# Revit family: NTO_ACCS_MorseTableAccessories-MA
name_source: partatom
category: Furniture
units: mm (PartAtom-declared; Revit-internal decimal feet)

## family parameters
Always vertical = Yes
Cut with Voids When Loaded = No
Enable Cutting in Views = No
OmniClass Number = 23.40.20.00
OmniClass Title = General Furniture and Specialties
Render Appearance Source = Family Geometry
Room Calculation Point = No
Shared = No
Work Plane-Based = Yes

## types (5) — shared parameters
AssetType = Movable
BIMObjectName = NTO_Morse_WorkTable
Category = Pr_65_70_11 : Cable management and accessories
Color = Available in 16 RALs
DurationUnit = year
ExpectedLife = 10
Features = Available in 16 RALs
Finish = Available in 16 RALs
IfcExportAs = IfcFurnitureType
IfcExportType = Table
MainColor = Available in 16 RALs
Manufacturer = NaughtOne
ManufacturerName = NaughtOne
ManufacturerURL = www.naughtone.com
Material = Available in 16 RALs
NBSDescription = Table
NBSReference = 45-35-72/352
ProductInformation = www.naughtone.com/product/morse/
Shape = Rectangular
URL = www.naughtone.com
Uniclass2015Code = Pr_65_70_11
Uniclass2015Title = Cable management and accessories
Uniclass2015Version = Products v1.30
Version = 1
WarrantyDescription = 10 Years
WarrantyDurationUnit = year
zero-valued in all types: Default Elevation

## per-type parameters (varying)
| type | Description | Dot Material | MABKE | MADOTS | MADOTT | MADSHS | MADVD | Model | ModelNumber | ModelReference | Name | NominalHeight | NominalLength | NominalWidth | Size | Type Comments |
| NTO_MorseTableAccessoriesCableManagementSmall_MADOTT | Morse Table Accessories - Cable Managment Small | NTO_Finish_PowderCoatOrange | No | No | Yes | No | No | MADOTT | MADOTT | Morse Table Accessories - Cable Managment Small | Morse Table Accessories - Cable Managment Small | 60 mm  [stored 0.19685 ft] | 70 mm  [stored 0.229659 ft] | 70 mm  [stored 0.229659 ft] | 70 x 70 x 60 mm | Morse Table Accessories - Cable Managment Small |
| NTO_MorseTableAccessoriesCableManagementLarge_MADOTS | Morse Table Accessories - Cable Managment Large | NTO_Finish_PowderCoatBlue | No | Yes | No | No | No | MADOTS | MADOTS | Morse Table Accessories - Cable Managment Large | Morse Table Accessories - Cable Managment Large | 100 mm  [stored 0.328084 ft] | 125 mm  [stored 0.410105 ft] | 125 mm  [stored 0.410105 ft] | 125 x 125 x 100 mm | Morse Table Accessories - Cable Managment Large |
| NTO_MorseTableAccessoriesCableManagementPillShaped_MADSHS | Morse Table Accessories - Cable Managment Pill Shaped | NTO_Finish_PowderCoatGrey | No | No | No | Yes | No | MADSHS | MADSHS | Morse Table Accessories - Cable Managment Pill Shaped | Morse Table Accessories - Cable Managment Pill Shaped | 70 mm  [stored 0.229659 ft] | 550 mm | 200 mm  [stored 0.656168 ft] | 550 x 250 x 70 mm | Morse Table Accessories - Cable Managment Pill Shaped |
| NTO_MorseTableAccessoriesPartitionPinBoard_MADVD | Morse Table Accessories - Partition Pin Board | NTO_Finish_PowderCoatGrey | No | No | No | No | Yes | MADVD | MADVD | Morse Table Accessories - Partition Pin Board | Morse Table Accessories - Partition Pin Board | 350 mm  [stored 1.14829 ft] | 600 mm | 150 mm  [stored 0.492126 ft] | 600 x 150 x 350 mm | Morse Table Accessories - Partition Pin Board |
| NTO_MorseTableAccessoriesBookEnd_MABKE | Morse Table Accessories - Book End | NTO_Finish_PowderCoatGrey | Yes | No | No | No | No | MABKE | MABKE | Morse Table Accessories - Book End | Morse Table Accessories - Book End | 150 mm  [stored 0.492126 ft] | 150 mm  [stored 0.492126 ft] | 80 mm  [stored 0.262467 ft] | 150 x 80 x 150 mm | Morse Table Accessories - Book End |

note: [stored X ft] marks values corroborated as IEEE doubles in the binary element streams (Revit-internal decimal feet)

## geometry (parser evidence)
native form markers: Sweep x2
no freeform markers — native parametric forms only
